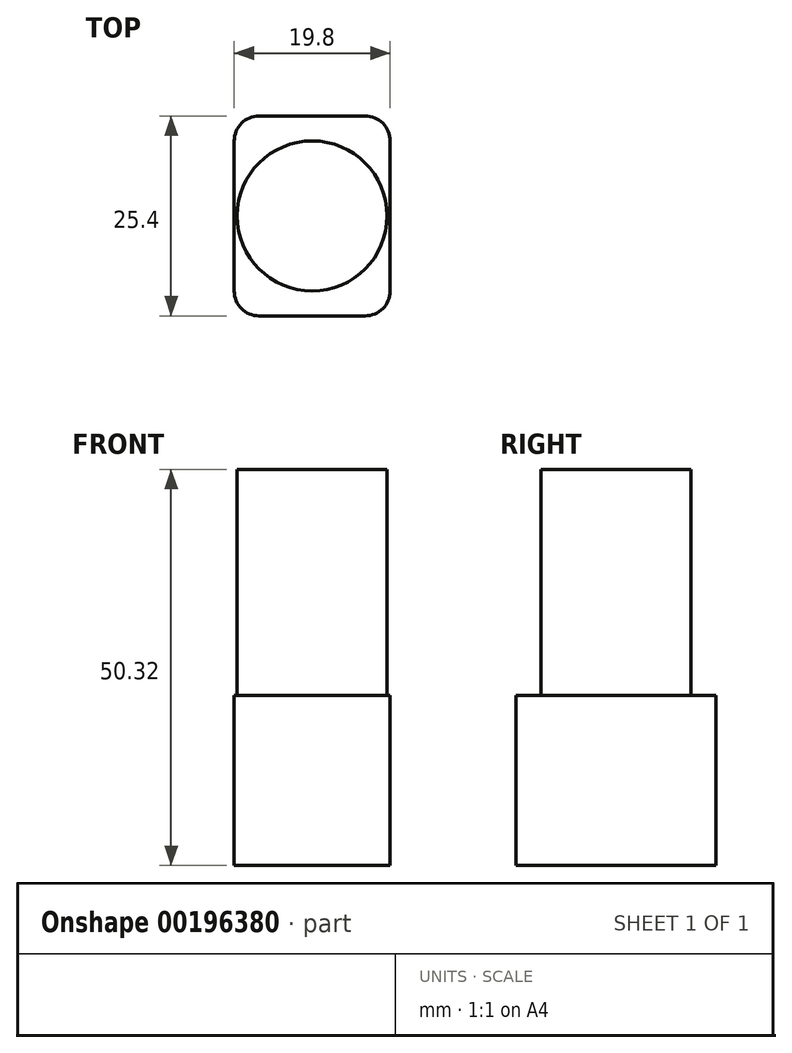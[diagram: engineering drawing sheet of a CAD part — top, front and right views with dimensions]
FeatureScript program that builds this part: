
annotation { "Feature Type Name" : "Feature", "Feature Type Description" : "" }
export const myFeature = defineFeature(function(context is Context, id is Id, definition is map)
    precondition{}
    {
        {
            var Q0;
            Q0=qCreatedBy(makeId("Top.planeOp"),FACE);
            var sketch = newSketch(context, id + "F0", { "sketchPlane" : qUnion([Q0])});
            skCircle(sketch, "E0", {"center": v(0, 0) * mm, "radius": 9.53 * mm});
            skSolve(sketch);
        }
        {
            var Q0;
            Q0 = qSketchRegion(id + "F0", true);
            extrude(context, id + "F1", {"entities" : qUnion([Q0]), "depth" : 28.73 * mm});
        }
        {
            var Q0;
            Q0=makeQuery(id+"F1.opExtrude","CAP_FACE",FACE,{"disambiguationData":[OSD([sQuery(id+"F0.wireOp",EDGE,"E0")])],"isStart":true});
            var sketch = newSketch(context, id + "F2", { "sketchPlane" : qUnion([Q0])});
            skLineSegment(sketch, "E1.bottom", {"start": v(9.9, 12.7) * mm, "end": v(-9.9, 12.7) * mm});
            skLineSegment(sketch, "E1.top", {"start": v(9.9, -12.7) * mm, "end": v(-9.9, -12.7) * mm});
            skLineSegment(sketch, "E1.left", {"start": v(9.9, 12.7) * mm, "end": v(9.9, -12.7) * mm});
            skLineSegment(sketch, "E1.right", {"start": v(-9.9, 12.7) * mm, "end": v(-9.9, -12.7) * mm});
            skPoint(sketch, "E1.middle", {"position": v(0, 0) * mm});
            skSolve(sketch);
        }
        {
            var Q0;
            Q0 = qSketchRegion(id + "F2", true);
            extrude(context, id + "F3", {"entities" : qUnion([Q0]), "operationType" : NewBodyOperationType.ADD, "depth" : 21.59 * mm});
        }
        {
            var Q0;
            Q0=makeQuery(id+"F3.opExtrude","SWEPT_EDGE",EDGE,{"disambiguationData":[OSD([sQuery(id+"F2.wireOp",EDGE,"E1.bottom"),sQuery(id+"F2.wireOp",EDGE,"E1.left")])]});
            var Q1;
            Q1=makeQuery(id+"F3.opExtrude","SWEPT_EDGE",EDGE,{"disambiguationData":[OSD([sQuery(id+"F2.wireOp",EDGE,"E1.bottom"),sQuery(id+"F2.wireOp",EDGE,"E1.right")])]});
            var Q2;
            Q2=makeQuery(id+"F3.opExtrude","SWEPT_EDGE",EDGE,{"disambiguationData":[OSD([sQuery(id+"F2.wireOp",EDGE,"E1.top"),sQuery(id+"F2.wireOp",EDGE,"E1.left")])]});
            var Q3;
            Q3=makeQuery(id+"F3.opExtrude","SWEPT_EDGE",EDGE,{"disambiguationData":[OSD([sQuery(id+"F2.wireOp",EDGE,"E1.top"),sQuery(id+"F2.wireOp",EDGE,"E1.right")])]});
            fillet(context, id + "F4", {"entities" : qUnion([Q0, Q1, Q2, Q3]), "radius" : 3.17 * mm, "tangentPropagation" : true, "allowEdgeOverflow" : false});
        }
    });
